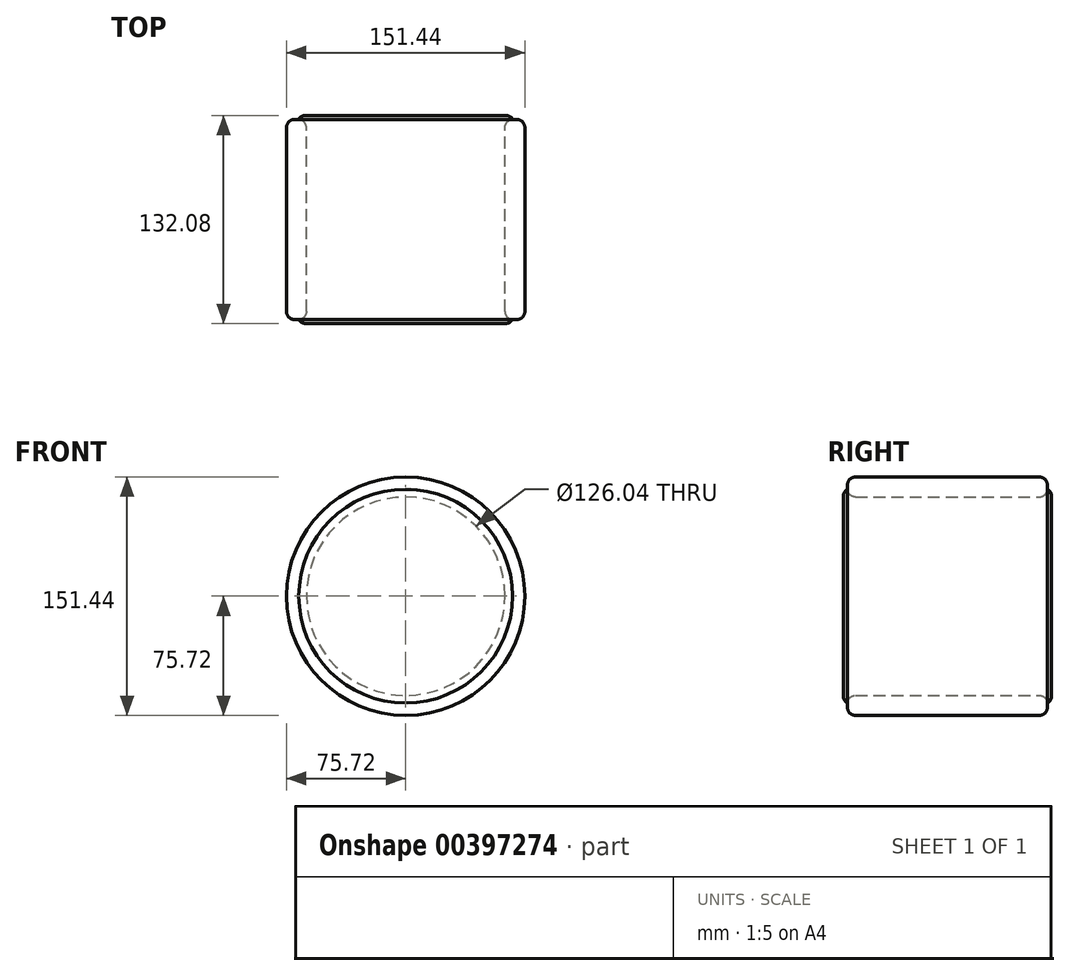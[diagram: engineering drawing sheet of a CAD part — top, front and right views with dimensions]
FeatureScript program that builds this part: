
annotation { "Feature Type Name" : "Feature", "Feature Type Description" : "" }
export const myFeature = defineFeature(function(context is Context, id is Id, definition is map)
    precondition{}
    {
        {
            var Q0;
            Q0=qCreatedBy(makeId("Front.planeOp"),FACE);
            var sketch = newSketch(context, id + "F0", { "sketchPlane" : qUnion([Q0])});
            skCircle(sketch, "E0", {"center": v(0, 0) * mm, "radius": 75.72 * mm});
            skSolve(sketch);
        }
        {
            var Q0;
            Q0=makeQuery(id+"F0.imprint","IMPRINT",FACE,{"disambiguationData":[TD([[makeQuery(id+"F0.imprint","IMPRINT",EDGE,{"derivedFrom":sQuery(id+"F0.wireOp",EDGE,"E0")}),1.0]])]});
            extrude(context, id + "F1", {"entities" : qUnion([Q0]), "depth" : 127 * mm});
        }
        {
            var Q0;
            Q0=makeQuery(id+"F1.opExtrude","CAP_FACE",FACE,{"disambiguationData":[OSD([sQuery(id+"F0.wireOp",EDGE,"E0")])],"isStart":false});
            shell(context, id + "F2", {"entities" : qUnion([Q0]), "thickness" : 12.7 * mm});
        }
        {
            var Q0;
            {var subQ0=sQuery(id+"F0.wireOp",EDGE,"E0");Q0=makeQuery(id+"F2.opShell","OFFSET_FACE",FACE,{"disambiguationData":[OSD([subQ0]),TDD([makeQuery(id+"F1.opExtrude","CAP_FACE",FACE,{"disambiguationData":[OSD([subQ0])],"isStart":true})])]});}
            extrude(context, id + "F3", {"entities" : qUnion([Q0]), "operationType" : NewBodyOperationType.REMOVE, "endBound" : BoundingType.THROUGH_ALL, "oppositeDirection" : true, "depth" : 25.4 * mm});
        }
        {
            var Q0;
            Q0=makeQuery(id+"F1.opExtrude","CAP_EDGE",EDGE,{"disambiguationData":[OSD([sQuery(id+"F0.wireOp",EDGE,"E0")])],"isStart":false});
            fillet(context, id + "F4", {"entities" : qUnion([Q0]), "radius" : 5.08 * mm, "tangentPropagation" : true, "allowEdgeOverflow" : false});
        }
        {
            var Q0;
            {var subQ0=sQuery(id+"F0.wireOp",EDGE,"E0");Q0=makeQuery(id+"F2.opShell","OFFSET_EDGE",EDGE,{"disambiguationData":[OSD([subQ0]),TDD([makeQuery(id+"F1.opExtrude","CAP_EDGE",EDGE,{"disambiguationData":[OSD([subQ0])],"isStart":false})])]});}
            fillet(context, id + "F5", {"entities" : qUnion([Q0]), "radius" : 5.08 * mm, "tangentPropagation" : true, "allowEdgeOverflow" : false});
        }
        {
            var Q0;
            Q0=makeQuery(id+"F1.opExtrude","CAP_EDGE",EDGE,{"disambiguationData":[OSD([sQuery(id+"F0.wireOp",EDGE,"E0")])],"isStart":true});
            fillet(context, id + "F6", {"entities" : qUnion([Q0]), "radius" : 5.08 * mm, "tangentPropagation" : true, "allowEdgeOverflow" : false});
        }
        {
            var Q0;
            {var subQ0=sQuery(id+"F0.wireOp",EDGE,"E0");Q0=makeQuery(id+"F3.boolean.opBoolean","INTERSECT",EDGE,{"derivedFrom":[makeQuery(id+"F1.opExtrude","CAP_FACE",FACE,{"disambiguationData":[OSD([subQ0])],"isStart":true}),makeQuery(id+"F3.opExtrude","SWEPT_FACE",FACE,{"disambiguationData":[OSD([subQ0])]})]});}
            fillet(context, id + "F7", {"entities" : qUnion([Q0]), "radius" : 5.08 * mm, "tangentPropagation" : true, "allowEdgeOverflow" : false});
        }
        {
            var Q0;
            Q0=makeQuery(id+"F1.opExtrude","CAP_FACE",FACE,{"disambiguationData":[OSD([sQuery(id+"F0.wireOp",EDGE,"E0")])],"isStart":true});
            var sketch = newSketch(context, id + "F8", { "sketchPlane" : qUnion([Q0])});
            skCircle(sketch, "E1", {"center": v(0, 0) * mm, "radius": 68.56 * mm});
            skSolve(sketch);
        }
        {
            var Q0;
            {var subQ0=sQuery(id+"F0.wireOp",EDGE,"E0");var subQ1=makeQuery(id+"F1.opExtrude","CAP_FACE",FACE,{"disambiguationData":[OSD([subQ0])],"isStart":true});Q0=makeQuery(id+"F8.imprint","IMPRINT",FACE,{"disambiguationData":[TD([[makeQuery(id+"F8.imprint","IMPRINT",EDGE,{"derivedFrom":makeQuery(id+"F7.opFillet","BLEND_EDGE",EDGE,{"blendedFrom":[makeQuery(id+"F3.boolean.opBoolean","INTERSECT",EDGE,{"derivedFrom":[subQ1,makeQuery(id+"F3.opExtrude","SWEPT_FACE",FACE,{"disambiguationData":[OSD([subQ0])]})]}),subQ1],"blendedInto":[subQ1]})}),-1.0]])]});}
            extrude(context, id + "F9", {"entities" : qUnion([Q0]), "depth" : 2.54 * mm});
        }
        {
            var Q0;
            Q0=makeQuery(id+"F1.opExtrude","CAP_FACE",FACE,{"disambiguationData":[OSD([sQuery(id+"F0.wireOp",EDGE,"E0")])],"isStart":false});
            var sketch = newSketch(context, id + "F10", { "sketchPlane" : qUnion([Q0])});
            skCircle(sketch, "E2", {"center": v(0, 0) * mm, "radius": 67.89 * mm});
            skSolve(sketch);
        }
        {
            var Q0;
            Q0=makeQuery(id+"F10.imprint","IMPRINT",FACE,{"disambiguationData":[TD([[makeQuery(id+"F10.imprint","IMPRINT",EDGE,{"derivedFrom":sQuery(id+"F10.wireOp",EDGE,"E2")}),1.0]])]});
            extrude(context, id + "F11", {"entities" : qUnion([Q0]), "depth" : 2.54 * mm});
        }
        {
            var Q0;
            Q0=makeQuery(id+"F11.opExtrude","CAP_FACE",FACE,{"disambiguationData":[OSD([sQuery(id+"F10.wireOp",EDGE,"E2")])],"isStart":false});
            fillet(context, id + "F12", {"entities" : qUnion([Q0]), "radius" : 5.08 * mm, "tangentPropagation" : true, "allowEdgeOverflow" : false});
        }
        {
            var Q0;
            Q0=makeQuery(id+"F9.opExtrude","CAP_FACE",FACE,{"disambiguationData":[OSD([sQuery(id+"F0.wireOp",EDGE,"E0")])],"isStart":false});
            fillet(context, id + "F13", {"entities" : qUnion([Q0]), "radius" : 5.08 * mm, "tangentPropagation" : true, "allowEdgeOverflow" : false});
        }
    });
